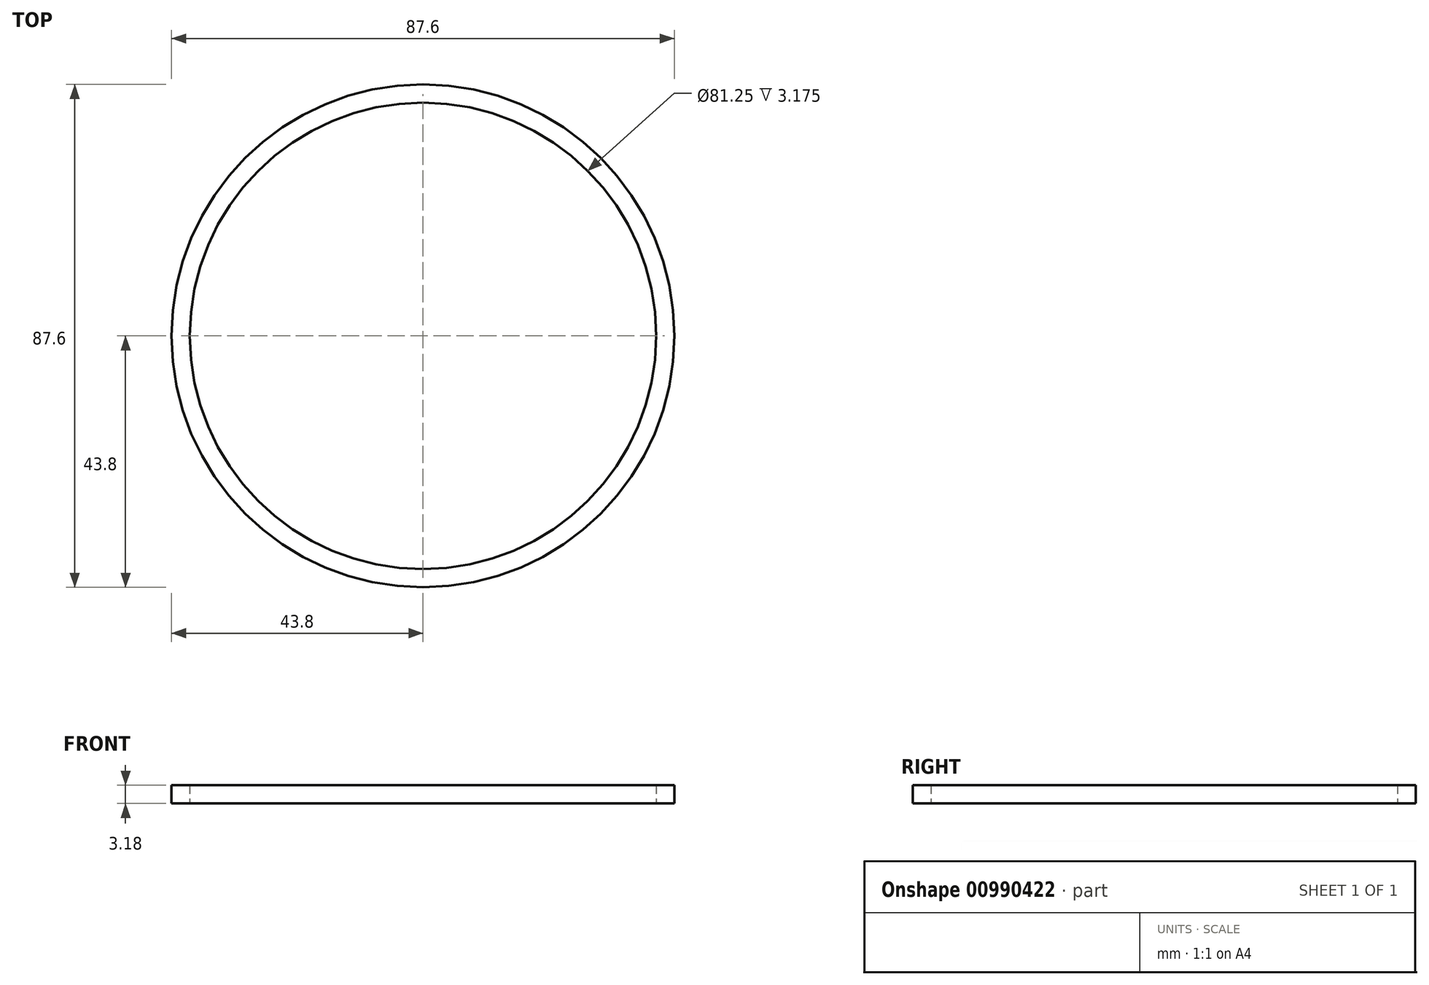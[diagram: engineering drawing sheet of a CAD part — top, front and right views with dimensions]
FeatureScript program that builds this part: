
annotation { "Feature Type Name" : "Feature", "Feature Type Description" : "" }
export const myFeature = defineFeature(function(context is Context, id is Id, definition is map)
    precondition{}
    {
        {
            var Q0;
            Q0=qCreatedBy(makeId("Top.planeOp"),FACE);
            var sketch = newSketch(context, id + "F0", { "sketchPlane" : qUnion([Q0])});
            skCircle(sketch, "E0", {"center": v(0, 0) * mm, "radius": 43.8 * mm});
            skCircle(sketch, "E1", {"center": v(0, 0) * mm, "radius": 40.63 * mm});
            skSolve(sketch);
        }
        {
            var Q0;
            Q0 = qSketchRegion(id + "F0", true);
            extrude(context, id + "F1", {"entities" : qUnion([Q0]), "depth" : 3.17 * mm, "offsetDistance" : 25.4 * mm});
        }
    });
